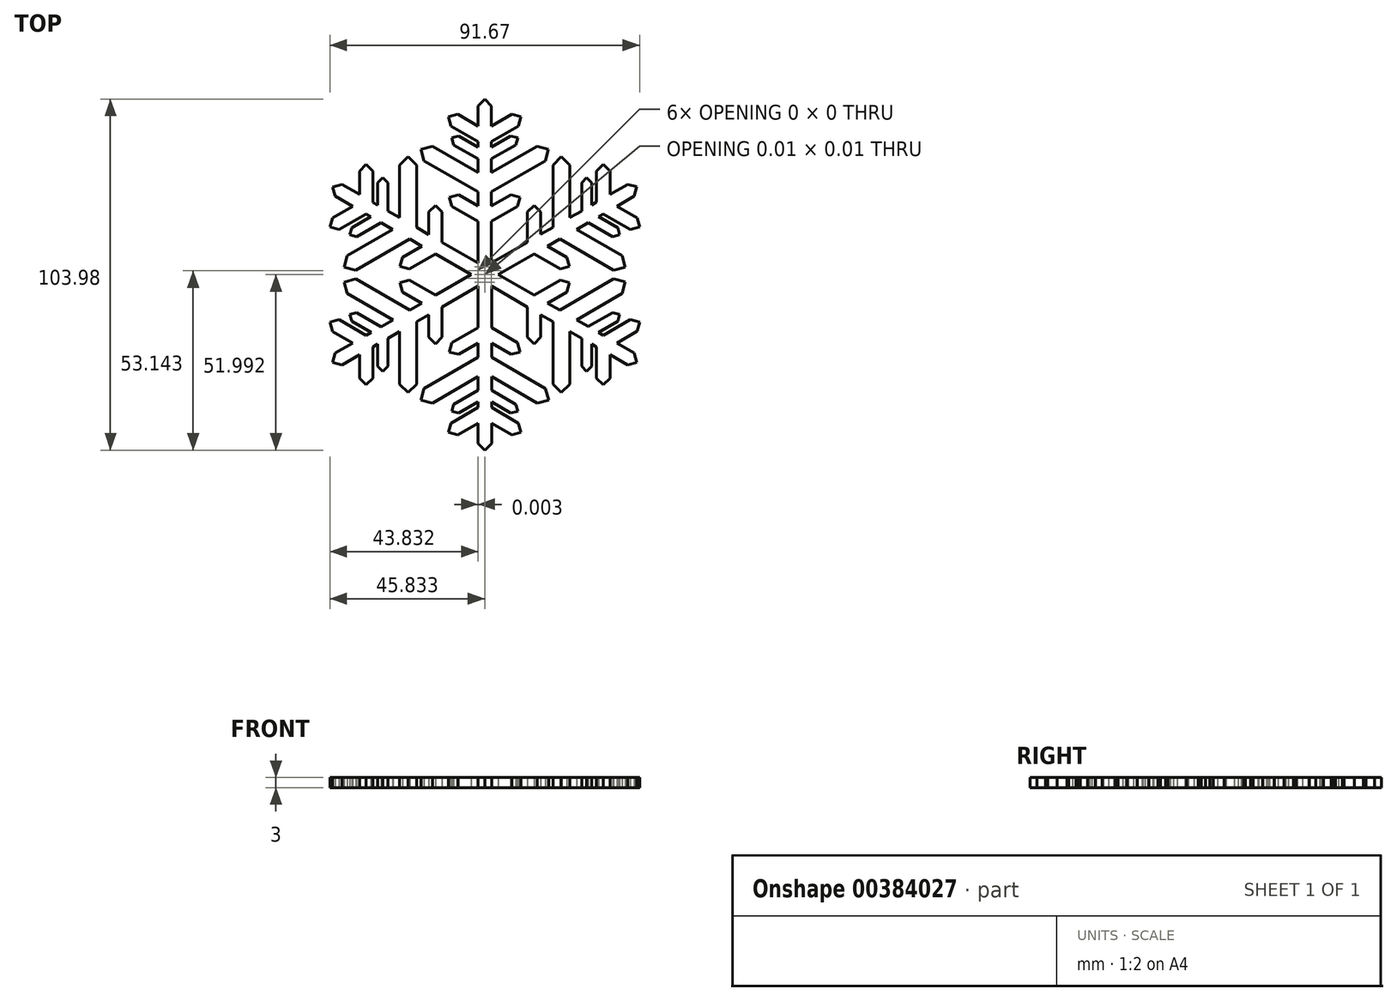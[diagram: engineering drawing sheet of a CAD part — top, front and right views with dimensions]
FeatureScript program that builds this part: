
annotation { "Feature Type Name" : "Feature", "Feature Type Description" : "" }
export const myFeature = defineFeature(function(context is Context, id is Id, definition is map)
    precondition{}
    {
        {
            var Q0;
            Q0=qCreatedBy(makeId("Top.planeOp"),FACE);
            var sketch = newSketch(context, id + "F0", { "sketchPlane" : qUnion([Q0])});
            skLineSegment(sketch, "E0", {"start": v(0, 26) * mm, "end": v(0, -26) * mm, "construction": true});
            skLineSegment(sketch, "E1", {"start": v(22.52, 13) * mm, "end": v(-22.52, -13) * mm, "construction": true});
            skLineSegment(sketch, "E2", {"start": v(22.52, -13) * mm, "end": v(-22.52, 13) * mm, "construction": true});
            skLineSegment(sketch, "E3", {"start": v(0, 0) * mm, "end": v(0, 26) * mm});
            skLineSegment(sketch, "E4", {"start": v(0, 26) * mm, "end": v(-1, 25) * mm});
            skLineSegment(sketch, "E5", {"start": v(-1, 25) * mm, "end": v(-1, 22) * mm});
            skLineSegment(sketch, "E6", {"start": v(-1, 22) * mm, "end": v(-4, 23.74) * mm});
            skLineSegment(sketch, "E7", {"start": v(-4, 23.74) * mm, "end": v(-5.37, 23.37) * mm});
            skLineSegment(sketch, "E8", {"start": v(-5.37, 23.37) * mm, "end": v(-5, 22) * mm});
            skLineSegment(sketch, "E9", {"start": v(-5, 22) * mm, "end": v(-1, 19.7) * mm});
            skLineSegment(sketch, "E10", {"start": v(-1, 19.7) * mm, "end": v(-1, 18.88) * mm});
            skLineSegment(sketch, "E11", {"start": v(-1, 18.88) * mm, "end": v(-3.86, 20.53) * mm});
            skLineSegment(sketch, "E12", {"start": v(-3.86, 20.53) * mm, "end": v(-4.88, 20.25) * mm});
            skLineSegment(sketch, "E13", {"start": v(-4.88, 20.25) * mm, "end": v(-4.6, 19.23) * mm});
            skLineSegment(sketch, "E14", {"start": v(-4.6, 19.23) * mm, "end": v(-1, 17.14) * mm});
            skLineSegment(sketch, "E15", {"start": v(-1, 17.14) * mm, "end": v(-1, 15.14) * mm});
            skLineSegment(sketch, "E16", {"start": v(-1, 15.14) * mm, "end": v(-7.74, 19.03) * mm});
            skLineSegment(sketch, "E17", {"start": v(-7.74, 19.03) * mm, "end": v(-9.45, 18.57) * mm});
            skLineSegment(sketch, "E18", {"start": v(-9.45, 18.57) * mm, "end": v(-9, 16.86) * mm});
            skLineSegment(sketch, "E19", {"start": v(-9, 16.86) * mm, "end": v(-1, 12.25) * mm});
            skLineSegment(sketch, "E20", {"start": v(-1, 12.25) * mm, "end": v(-1, 10.17) * mm});
            skLineSegment(sketch, "E21", {"start": v(-1, 10.17) * mm, "end": v(-3.87, 11.83) * mm});
            skLineSegment(sketch, "E22", {"start": v(-3.87, 11.83) * mm, "end": v(-5.23, 11.47) * mm});
            skLineSegment(sketch, "E23", {"start": v(-5.23, 11.47) * mm, "end": v(-4.87, 10.1) * mm});
            skLineSegment(sketch, "E24", {"start": v(-4.87, 10.1) * mm, "end": v(-1, 7.87) * mm});
            skLineSegment(sketch, "E25", {"start": v(-1, 7.87) * mm, "end": v(-1, 0.58) * mm});
            skLineSegment(sketch, "E26.MirrorCS", {"start": v(4.88, 20.25) * mm, "end": v(4.6, 19.23) * mm});
            skLineSegment(sketch, "E27.MirrorCS", {"start": v(5.23, 11.47) * mm, "end": v(4.87, 10.1) * mm});
            skLineSegment(sketch, "E28.MirrorCS", {"start": v(3.86, 20.53) * mm, "end": v(4.88, 20.25) * mm});
            skLineSegment(sketch, "E29.MirrorCS", {"start": v(1, 15.14) * mm, "end": v(7.74, 19.03) * mm});
            skLineSegment(sketch, "E30.MirrorCS", {"start": v(4.87, 10.1) * mm, "end": v(1, 7.87) * mm});
            skLineSegment(sketch, "E31.MirrorCS", {"start": v(1, 10.17) * mm, "end": v(3.87, 11.83) * mm});
            skLineSegment(sketch, "E32.MirrorCS", {"start": v(1, 17.14) * mm, "end": v(1, 15.14) * mm});
            skLineSegment(sketch, "E33.MirrorCS", {"start": v(4.6, 19.23) * mm, "end": v(1, 17.14) * mm});
            skLineSegment(sketch, "E34.MirrorCS", {"start": v(9.45, 18.57) * mm, "end": v(9, 16.86) * mm});
            skLineSegment(sketch, "E35.MirrorCS", {"start": v(1, 12.25) * mm, "end": v(1, 10.17) * mm});
            skLineSegment(sketch, "E36.MirrorCS", {"start": v(9, 16.86) * mm, "end": v(1, 12.25) * mm});
            skLineSegment(sketch, "E37.MirrorCS", {"start": v(0, 26) * mm, "end": v(1, 25) * mm});
            skLineSegment(sketch, "E38.MirrorCS", {"start": v(1, 22) * mm, "end": v(4, 23.74) * mm});
            skLineSegment(sketch, "E39.MirrorCS", {"start": v(1, 25) * mm, "end": v(1, 22) * mm});
            skLineSegment(sketch, "E40.MirrorCS", {"start": v(7.74, 19.03) * mm, "end": v(9.45, 18.57) * mm});
            skLineSegment(sketch, "E41.MirrorCS", {"start": v(1, 18.88) * mm, "end": v(3.86, 20.53) * mm});
            skLineSegment(sketch, "E42.MirrorCS", {"start": v(4, 23.74) * mm, "end": v(5.37, 23.37) * mm});
            skLineSegment(sketch, "E43.MirrorCS", {"start": v(5, 22) * mm, "end": v(1, 19.7) * mm});
            skLineSegment(sketch, "E44.MirrorCS", {"start": v(5.37, 23.37) * mm, "end": v(5, 22) * mm});
            skLineSegment(sketch, "E45.MirrorCS", {"start": v(1, 7.87) * mm, "end": v(1, 0.58) * mm});
            skLineSegment(sketch, "E46.MirrorCS", {"start": v(3.87, 11.83) * mm, "end": v(5.23, 11.47) * mm});
            skLineSegment(sketch, "E47.MirrorCS", {"start": v(1, 19.7) * mm, "end": v(1, 18.88) * mm});
            skLineSegment(sketch, "E48", {"start": v(-5, 22) * mm, "end": v(-4, 23.74) * mm, "construction": true});
            skLineSegment(sketch, "E49", {"start": v(-4.6, 19.23) * mm, "end": v(-3.86, 20.53) * mm, "construction": true});
            skLineSegment(sketch, "E50", {"start": v(-9, 16.86) * mm, "end": v(-7.74, 19.03) * mm, "construction": true});
            skLineSegment(sketch, "E51", {"start": v(-4.87, 10.1) * mm, "end": v(-3.87, 11.83) * mm, "construction": true});
            skLineSegment(sketch, "E52", {"start": v(-9.45, 18.57) * mm, "end": v(-8.37, 17.95) * mm, "construction": true});
            skLineSegment(sketch, "E53", {"start": v(-4.37, 10.97) * mm, "end": v(-5.23, 11.47) * mm, "construction": true});
            skLineSegment(sketch, "E54", {"start": v(-4.23, 19.88) * mm, "end": v(-4.88, 20.25) * mm, "construction": true});
            skLineSegment(sketch, "E55", {"start": v(-4.5, 22.87) * mm, "end": v(-5.37, 23.37) * mm, "construction": true});
            skLineSegment(sketch, "E56.1.0", {"start": v(-16.55, 15.33) * mm, "end": v(-16.55, 10.72) * mm});
            skLineSegment(sketch, "E56.1.1", {"start": v(-14.34, 9.44) * mm, "end": v(-12.6, 8.44) * mm});
            skLineSegment(sketch, "E56.1.2", {"start": v(-21.55, 6.67) * mm, "end": v(-17.55, 8.98) * mm});
            skLineSegment(sketch, "E56.1.3", {"start": v(-16.55, 10.72) * mm, "end": v(-15.84, 10.3) * mm});
            skLineSegment(sketch, "E56.1.4", {"start": v(-11.35, 17.47) * mm, "end": v(-10.1, 16.22) * mm});
            skLineSegment(sketch, "E56.1.5", {"start": v(-18.55, 15.33) * mm, "end": v(-17.55, 16.33) * mm});
            skLineSegment(sketch, "E56.1.6", {"start": v(-17.55, 16.33) * mm, "end": v(-16.55, 15.33) * mm});
            skLineSegment(sketch, "E56.1.7", {"start": v(-12.6, 16.22) * mm, "end": v(-11.35, 17.47) * mm});
            skLineSegment(sketch, "E56.1.8", {"start": v(-11.17, 0.83) * mm, "end": v(-7.3, 3.07) * mm});
            skLineSegment(sketch, "E56.1.9", {"start": v(-8.3, 9.27) * mm, "end": v(-7.3, 10.27) * mm});
            skLineSegment(sketch, "E56.1.10", {"start": v(-6.3, 9.27) * mm, "end": v(-6.3, 4.8) * mm});
            skLineSegment(sketch, "E56.1.11", {"start": v(-22.55, 8.4) * mm, "end": v(-22.92, 7.04) * mm});
            skLineSegment(sketch, "E56.1.12", {"start": v(-22.92, 7.04) * mm, "end": v(-21.55, 6.67) * mm});
            skLineSegment(sketch, "E56.1.13", {"start": v(-17.55, 8.98) * mm, "end": v(-16.84, 8.57) * mm});
            skLineSegment(sketch, "E56.1.14", {"start": v(-10.1, 16.22) * mm, "end": v(-10.1, 7) * mm});
            skLineSegment(sketch, "E56.1.15", {"start": v(-12.54, 1.2) * mm, "end": v(-11.17, 0.83) * mm});
            skLineSegment(sketch, "E56.1.16", {"start": v(-19.55, 10.14) * mm, "end": v(-22.55, 8.4) * mm});
            skLineSegment(sketch, "E56.1.17", {"start": v(-14.34, 13.6) * mm, "end": v(-14.34, 9.44) * mm});
            skLineSegment(sketch, "E56.1.18", {"start": v(-13.6, 6.7) * mm, "end": v(-20.34, 2.81) * mm});
            skLineSegment(sketch, "E56.1.19", {"start": v(-7.3, 3.07) * mm, "end": v(-1, -0.58) * mm});
            skLineSegment(sketch, "E56.1.20", {"start": v(-15.34, 7.7) * mm, "end": v(-13.6, 6.7) * mm});
            skLineSegment(sketch, "E56.1.21", {"start": v(-16.84, 8.57) * mm, "end": v(-19.7, 6.92) * mm});
            skLineSegment(sketch, "E56.1.22", {"start": v(-8.3, 5.96) * mm, "end": v(-8.3, 9.27) * mm});
            skLineSegment(sketch, "E56.1.23", {"start": v(-11.1, 5.26) * mm, "end": v(-9.3, 4.22) * mm});
            skLineSegment(sketch, "E56.1.24", {"start": v(-12.6, 8.44) * mm, "end": v(-12.6, 16.22) * mm});
            skLineSegment(sketch, "E56.1.25", {"start": v(-19.1, 0.65) * mm, "end": v(-11.1, 5.26) * mm});
            skLineSegment(sketch, "E56.1.26", {"start": v(-20.8, 1.1) * mm, "end": v(-19.1, 0.65) * mm});
            skLineSegment(sketch, "E56.1.27", {"start": v(-21.14, 13.37) * mm, "end": v(-18.55, 11.87) * mm});
            skLineSegment(sketch, "E56.1.28", {"start": v(-10.1, 7) * mm, "end": v(-8.3, 5.96) * mm});
            skLineSegment(sketch, "E56.1.29", {"start": v(-7.3, 10.27) * mm, "end": v(-6.3, 9.27) * mm});
            skLineSegment(sketch, "E56.1.30", {"start": v(-18.55, 11.87) * mm, "end": v(-18.55, 15.33) * mm});
            skLineSegment(sketch, "E56.1.31", {"start": v(-15.84, 10.3) * mm, "end": v(-15.84, 13.6) * mm});
            skLineSegment(sketch, "E56.1.32", {"start": v(-12.17, 2.57) * mm, "end": v(-12.54, 1.2) * mm});
            skLineSegment(sketch, "E56.1.33", {"start": v(-20.34, 2.81) * mm, "end": v(-20.8, 1.1) * mm});
            skLineSegment(sketch, "E56.1.34", {"start": v(-9.3, 4.22) * mm, "end": v(-12.17, 2.57) * mm});
            skLineSegment(sketch, "E56.1.35", {"start": v(-18.95, 5.63) * mm, "end": v(-15.34, 7.7) * mm});
            skLineSegment(sketch, "E56.1.36", {"start": v(-6.3, 4.8) * mm, "end": v(0, 1.16) * mm});
            skLineSegment(sketch, "E56.1.37", {"start": v(-22.14, 11.64) * mm, "end": v(-19.55, 10.14) * mm});
            skLineSegment(sketch, "E56.1.38", {"start": v(0, 0) * mm, "end": v(-22.51, 13) * mm});
            skLineSegment(sketch, "E56.1.39", {"start": v(-20.8, 1.1) * mm, "end": v(-19.72, 1.73) * mm, "construction": true});
            skLineSegment(sketch, "E56.1.40", {"start": v(-18.95, 5.63) * mm, "end": v(-19.7, 6.92) * mm, "construction": true});
            skLineSegment(sketch, "E56.1.41", {"start": v(-11.67, 1.7) * mm, "end": v(-12.54, 1.2) * mm, "construction": true});
            skLineSegment(sketch, "E56.1.42", {"start": v(-21.55, 6.67) * mm, "end": v(-22.55, 8.4) * mm, "construction": true});
            skLineSegment(sketch, "E56.1.43", {"start": v(-19.32, 6.28) * mm, "end": v(-19.97, 5.9) * mm, "construction": true});
            skLineSegment(sketch, "E56.1.44", {"start": v(-11.17, 0.83) * mm, "end": v(-12.17, 2.57) * mm, "construction": true});
            skLineSegment(sketch, "E56.1.45", {"start": v(-19.1, 0.65) * mm, "end": v(-20.34, 2.81) * mm, "construction": true});
            skLineSegment(sketch, "E56.1.46", {"start": v(-22.05, 7.54) * mm, "end": v(-22.92, 7.04) * mm, "construction": true});
            skLineSegment(sketch, "E56.1.47", {"start": v(-15.1, 14.35) * mm, "end": v(-14.34, 13.6) * mm});
            skLineSegment(sketch, "E56.1.48", {"start": v(-15.84, 13.6) * mm, "end": v(-15.1, 14.35) * mm});
            skLineSegment(sketch, "E56.1.49", {"start": v(-22.51, 13) * mm, "end": v(-21.14, 13.37) * mm});
            skLineSegment(sketch, "E56.1.50", {"start": v(-22.51, 13) * mm, "end": v(-22.14, 11.64) * mm});
            skLineSegment(sketch, "E56.1.51", {"start": v(-19.97, 5.9) * mm, "end": v(-18.95, 5.63) * mm});
            skLineSegment(sketch, "E56.1.52", {"start": v(-19.7, 6.92) * mm, "end": v(-19.97, 5.9) * mm});
            skLineSegment(sketch, "E56.2.0", {"start": v(-21.55, -6.66) * mm, "end": v(-17.55, -8.97) * mm});
            skLineSegment(sketch, "E56.2.1", {"start": v(-15.34, -7.7) * mm, "end": v(-13.6, -6.7) * mm});
            skLineSegment(sketch, "E56.2.2", {"start": v(-16.55, -15.33) * mm, "end": v(-16.55, -10.7) * mm});
            skLineSegment(sketch, "E56.2.3", {"start": v(-17.55, -8.97) * mm, "end": v(-16.84, -8.56) * mm});
            skLineSegment(sketch, "E56.2.4", {"start": v(-20.8, -1.1) * mm, "end": v(-19.1, -0.64) * mm});
            skLineSegment(sketch, "E56.2.5", {"start": v(-22.55, -8.4) * mm, "end": v(-22.92, -7.03) * mm});
            skLineSegment(sketch, "E56.2.6", {"start": v(-22.92, -7.03) * mm, "end": v(-21.55, -6.66) * mm});
            skLineSegment(sketch, "E56.2.7", {"start": v(-20.34, -2.8) * mm, "end": v(-20.8, -1.1) * mm});
            skLineSegment(sketch, "E56.2.8", {"start": v(-6.3, -9.26) * mm, "end": v(-6.3, -4.8) * mm});
            skLineSegment(sketch, "E56.2.9", {"start": v(-12.17, -2.56) * mm, "end": v(-12.54, -1.2) * mm});
            skLineSegment(sketch, "E56.2.10", {"start": v(-11.17, -0.83) * mm, "end": v(-7.3, -3.06) * mm});
            skLineSegment(sketch, "E56.2.11", {"start": v(-18.55, -15.33) * mm, "end": v(-17.55, -16.33) * mm});
            skLineSegment(sketch, "E56.2.12", {"start": v(-17.55, -16.33) * mm, "end": v(-16.55, -15.33) * mm});
            skLineSegment(sketch, "E56.2.13", {"start": v(-16.55, -10.7) * mm, "end": v(-15.84, -10.3) * mm});
            skLineSegment(sketch, "E56.2.14", {"start": v(-19.1, -0.64) * mm, "end": v(-11.1, -5.25) * mm});
            skLineSegment(sketch, "E56.2.15", {"start": v(-7.3, -10.26) * mm, "end": v(-6.3, -9.26) * mm});
            skLineSegment(sketch, "E56.2.16", {"start": v(-18.55, -11.86) * mm, "end": v(-18.55, -15.33) * mm});
            skLineSegment(sketch, "E56.2.17", {"start": v(-18.95, -5.62) * mm, "end": v(-15.34, -7.7) * mm});
            skLineSegment(sketch, "E56.2.18", {"start": v(-12.6, -8.43) * mm, "end": v(-12.6, -16.2) * mm});
            skLineSegment(sketch, "E56.2.19", {"start": v(-6.3, -4.8) * mm, "end": v(0, -1.15) * mm});
            skLineSegment(sketch, "E56.2.20", {"start": v(-14.34, -9.43) * mm, "end": v(-12.6, -8.43) * mm});
            skLineSegment(sketch, "E56.2.21", {"start": v(-15.84, -10.3) * mm, "end": v(-15.84, -13.6) * mm});
            skLineSegment(sketch, "E56.2.22", {"start": v(-9.3, -4.21) * mm, "end": v(-12.17, -2.56) * mm});
            skLineSegment(sketch, "E56.2.23", {"start": v(-10.1, -6.98) * mm, "end": v(-8.3, -5.95) * mm});
            skLineSegment(sketch, "E56.2.24", {"start": v(-13.6, -6.7) * mm, "end": v(-20.34, -2.8) * mm});
            skLineSegment(sketch, "E56.2.25", {"start": v(-10.1, -16.2) * mm, "end": v(-10.1, -6.98) * mm});
            skLineSegment(sketch, "E56.2.26", {"start": v(-11.35, -17.46) * mm, "end": v(-10.1, -16.2) * mm});
            skLineSegment(sketch, "E56.2.27", {"start": v(-22.14, -11.63) * mm, "end": v(-19.55, -10.13) * mm});
            skLineSegment(sketch, "E56.2.28", {"start": v(-11.1, -5.25) * mm, "end": v(-9.3, -4.21) * mm});
            skLineSegment(sketch, "E56.2.29", {"start": v(-12.54, -1.2) * mm, "end": v(-11.17, -0.83) * mm});
            skLineSegment(sketch, "E56.2.30", {"start": v(-19.55, -10.13) * mm, "end": v(-22.55, -8.4) * mm});
            skLineSegment(sketch, "E56.2.31", {"start": v(-16.84, -8.56) * mm, "end": v(-19.7, -6.92) * mm});
            skLineSegment(sketch, "E56.2.32", {"start": v(-8.3, -9.26) * mm, "end": v(-7.3, -10.26) * mm});
            skLineSegment(sketch, "E56.2.33", {"start": v(-12.6, -16.2) * mm, "end": v(-11.35, -17.46) * mm});
            skLineSegment(sketch, "E56.2.34", {"start": v(-8.3, -5.95) * mm, "end": v(-8.3, -9.26) * mm});
            skLineSegment(sketch, "E56.2.35", {"start": v(-14.34, -13.6) * mm, "end": v(-14.34, -9.43) * mm});
            skLineSegment(sketch, "E56.2.36", {"start": v(-7.3, -3.06) * mm, "end": v(-1, 0.59) * mm});
            skLineSegment(sketch, "E56.2.37", {"start": v(-21.14, -13.36) * mm, "end": v(-18.55, -11.86) * mm});
            skLineSegment(sketch, "E56.2.38", {"start": v(0, 0) * mm, "end": v(-22.5, -13) * mm});
            skLineSegment(sketch, "E56.2.39", {"start": v(-11.35, -17.46) * mm, "end": v(-11.35, -16.2) * mm, "construction": true});
            skLineSegment(sketch, "E56.2.40", {"start": v(-14.34, -13.6) * mm, "end": v(-15.84, -13.6) * mm, "construction": true});
            skLineSegment(sketch, "E56.2.41", {"start": v(-7.3, -9.26) * mm, "end": v(-7.3, -10.26) * mm, "construction": true});
            skLineSegment(sketch, "E56.2.42", {"start": v(-16.55, -15.33) * mm, "end": v(-18.55, -15.33) * mm, "construction": true});
            skLineSegment(sketch, "E56.2.43", {"start": v(-15.09, -13.6) * mm, "end": v(-15.09, -14.34) * mm, "construction": true});
            skLineSegment(sketch, "E56.2.44", {"start": v(-6.3, -9.26) * mm, "end": v(-8.3, -9.26) * mm, "construction": true});
            skLineSegment(sketch, "E56.2.45", {"start": v(-10.1, -16.2) * mm, "end": v(-12.6, -16.2) * mm, "construction": true});
            skLineSegment(sketch, "E56.2.46", {"start": v(-17.55, -15.33) * mm, "end": v(-17.55, -16.33) * mm, "construction": true});
            skLineSegment(sketch, "E56.2.47", {"start": v(-19.97, -5.9) * mm, "end": v(-18.95, -5.62) * mm});
            skLineSegment(sketch, "E56.2.48", {"start": v(-19.7, -6.92) * mm, "end": v(-19.97, -5.9) * mm});
            skLineSegment(sketch, "E56.2.49", {"start": v(-22.5, -13) * mm, "end": v(-22.14, -11.63) * mm});
            skLineSegment(sketch, "E56.2.50", {"start": v(-22.5, -13) * mm, "end": v(-21.14, -13.36) * mm});
            skLineSegment(sketch, "E56.2.51", {"start": v(-15.09, -14.34) * mm, "end": v(-14.34, -13.6) * mm});
            skLineSegment(sketch, "E56.2.52", {"start": v(-15.84, -13.6) * mm, "end": v(-15.09, -14.34) * mm});
            skLineSegment(sketch, "E56.3.0", {"start": v(-5, -22) * mm, "end": v(-1, -19.68) * mm});
            skLineSegment(sketch, "E56.3.1", {"start": v(-1, -17.13) * mm, "end": v(-1, -15.12) * mm});
            skLineSegment(sketch, "E56.3.2", {"start": v(5, -22) * mm, "end": v(1, -19.68) * mm});
            skLineSegment(sketch, "E56.3.3", {"start": v(-1, -19.68) * mm, "end": v(-1, -18.86) * mm});
            skLineSegment(sketch, "E56.3.4", {"start": v(-9.44, -18.56) * mm, "end": v(-8.99, -16.85) * mm});
            skLineSegment(sketch, "E56.3.5", {"start": v(-4, -23.73) * mm, "end": v(-5.36, -23.36) * mm});
            skLineSegment(sketch, "E56.3.6", {"start": v(-5.36, -23.36) * mm, "end": v(-5, -22) * mm});
            skLineSegment(sketch, "E56.3.7", {"start": v(-7.74, -19.02) * mm, "end": v(-9.44, -18.56) * mm});
            skLineSegment(sketch, "E56.3.8", {"start": v(4.87, -10.09) * mm, "end": v(1, -7.85) * mm});
            skLineSegment(sketch, "E56.3.9", {"start": v(-3.87, -11.82) * mm, "end": v(-5.23, -11.45) * mm});
            skLineSegment(sketch, "E56.3.10", {"start": v(-4.87, -10.09) * mm, "end": v(-1, -7.85) * mm});
            skLineSegment(sketch, "E56.3.11", {"start": v(4, -23.73) * mm, "end": v(5.37, -23.36) * mm});
            skLineSegment(sketch, "E56.3.12", {"start": v(5.37, -23.36) * mm, "end": v(5, -22) * mm});
            skLineSegment(sketch, "E56.3.13", {"start": v(1, -19.68) * mm, "end": v(1, -18.86) * mm});
            skLineSegment(sketch, "E56.3.14", {"start": v(-8.99, -16.85) * mm, "end": v(-1, -12.24) * mm});
            skLineSegment(sketch, "E56.3.15", {"start": v(5.24, -11.45) * mm, "end": v(4.87, -10.09) * mm});
            skLineSegment(sketch, "E56.3.16", {"start": v(1, -22) * mm, "end": v(4, -23.73) * mm});
            skLineSegment(sketch, "E56.3.17", {"start": v(-4.6, -19.21) * mm, "end": v(-1, -17.13) * mm});
            skLineSegment(sketch, "E56.3.18", {"start": v(1, -15.12) * mm, "end": v(7.74, -19.02) * mm});
            skLineSegment(sketch, "E56.3.19", {"start": v(1, -7.85) * mm, "end": v(1, -0.57) * mm});
            skLineSegment(sketch, "E56.3.20", {"start": v(1, -17.13) * mm, "end": v(1, -15.12) * mm});
            skLineSegment(sketch, "E56.3.21", {"start": v(1, -18.86) * mm, "end": v(3.86, -20.51) * mm});
            skLineSegment(sketch, "E56.3.22", {"start": v(-1, -10.16) * mm, "end": v(-3.87, -11.82) * mm});
            skLineSegment(sketch, "E56.3.23", {"start": v(1, -12.24) * mm, "end": v(1, -10.16) * mm});
            skLineSegment(sketch, "E56.3.24", {"start": v(-1, -15.12) * mm, "end": v(-7.74, -19.02) * mm});
            skLineSegment(sketch, "E56.3.25", {"start": v(9, -16.85) * mm, "end": v(1, -12.24) * mm});
            skLineSegment(sketch, "E56.3.26", {"start": v(9.45, -18.56) * mm, "end": v(9, -16.85) * mm});
            skLineSegment(sketch, "E56.3.27", {"start": v(-1, -24.99) * mm, "end": v(-1, -22) * mm});
            skLineSegment(sketch, "E56.3.28", {"start": v(-1, -12.24) * mm, "end": v(-1, -10.16) * mm});
            skLineSegment(sketch, "E56.3.29", {"start": v(-5.23, -11.45) * mm, "end": v(-4.87, -10.09) * mm});
            skLineSegment(sketch, "E56.3.30", {"start": v(-1, -22) * mm, "end": v(-4, -23.73) * mm});
            skLineSegment(sketch, "E56.3.31", {"start": v(-1, -18.86) * mm, "end": v(-3.85, -20.51) * mm});
            skLineSegment(sketch, "E56.3.32", {"start": v(3.87, -11.82) * mm, "end": v(5.24, -11.45) * mm});
            skLineSegment(sketch, "E56.3.33", {"start": v(7.74, -19.02) * mm, "end": v(9.45, -18.56) * mm});
            skLineSegment(sketch, "E56.3.34", {"start": v(1, -10.16) * mm, "end": v(3.87, -11.82) * mm});
            skLineSegment(sketch, "E56.3.35", {"start": v(4.6, -19.21) * mm, "end": v(1, -17.13) * mm});
            skLineSegment(sketch, "E56.3.36", {"start": v(-1, -7.85) * mm, "end": v(-1, -0.57) * mm});
            skLineSegment(sketch, "E56.3.37", {"start": v(1, -24.99) * mm, "end": v(1, -22) * mm});
            skLineSegment(sketch, "E56.3.38", {"start": v(0, 0.01) * mm, "end": v(0, -25.99) * mm});
            skLineSegment(sketch, "E56.3.39", {"start": v(9.45, -18.56) * mm, "end": v(8.37, -17.93) * mm, "construction": true});
            skLineSegment(sketch, "E56.3.40", {"start": v(4.6, -19.21) * mm, "end": v(3.86, -20.51) * mm, "construction": true});
            skLineSegment(sketch, "E56.3.41", {"start": v(4.37, -10.95) * mm, "end": v(5.24, -11.45) * mm, "construction": true});
            skLineSegment(sketch, "E56.3.42", {"start": v(5, -22) * mm, "end": v(4, -23.73) * mm, "construction": true});
            skLineSegment(sketch, "E56.3.43", {"start": v(4.23, -19.86) * mm, "end": v(4.88, -20.24) * mm, "construction": true});
            skLineSegment(sketch, "E56.3.44", {"start": v(4.87, -10.09) * mm, "end": v(3.87, -11.82) * mm, "construction": true});
            skLineSegment(sketch, "E56.3.45", {"start": v(9, -16.85) * mm, "end": v(7.74, -19.02) * mm, "construction": true});
            skLineSegment(sketch, "E56.3.46", {"start": v(4.5, -22.86) * mm, "end": v(5.37, -23.36) * mm, "construction": true});
            skLineSegment(sketch, "E56.3.47", {"start": v(-4.88, -20.24) * mm, "end": v(-4.6, -19.21) * mm});
            skLineSegment(sketch, "E56.3.48", {"start": v(-3.85, -20.51) * mm, "end": v(-4.88, -20.24) * mm});
            skLineSegment(sketch, "E56.3.49", {"start": v(0, -25.99) * mm, "end": v(-1, -24.99) * mm});
            skLineSegment(sketch, "E56.3.50", {"start": v(0, -25.99) * mm, "end": v(1, -24.99) * mm});
            skLineSegment(sketch, "E56.3.51", {"start": v(4.88, -20.24) * mm, "end": v(4.6, -19.21) * mm});
            skLineSegment(sketch, "E56.3.52", {"start": v(3.86, -20.51) * mm, "end": v(4.88, -20.24) * mm});
            skLineSegment(sketch, "E56.4.0", {"start": v(16.55, -15.32) * mm, "end": v(16.55, -10.7) * mm});
            skLineSegment(sketch, "E56.4.1", {"start": v(14.34, -9.43) * mm, "end": v(12.6, -8.42) * mm});
            skLineSegment(sketch, "E56.4.2", {"start": v(21.55, -6.66) * mm, "end": v(17.55, -8.97) * mm});
            skLineSegment(sketch, "E56.4.3", {"start": v(16.55, -10.7) * mm, "end": v(15.84, -10.3) * mm});
            skLineSegment(sketch, "E56.4.4", {"start": v(11.36, -17.46) * mm, "end": v(10.1, -16.2) * mm});
            skLineSegment(sketch, "E56.4.5", {"start": v(18.55, -15.32) * mm, "end": v(17.55, -16.32) * mm});
            skLineSegment(sketch, "E56.4.6", {"start": v(17.55, -16.32) * mm, "end": v(16.55, -15.32) * mm});
            skLineSegment(sketch, "E56.4.7", {"start": v(12.6, -16.2) * mm, "end": v(11.36, -17.46) * mm});
            skLineSegment(sketch, "E56.4.8", {"start": v(11.18, -0.82) * mm, "end": v(7.3, -3.06) * mm});
            skLineSegment(sketch, "E56.4.9", {"start": v(8.3, -9.26) * mm, "end": v(7.3, -10.26) * mm});
            skLineSegment(sketch, "E56.4.10", {"start": v(6.3, -9.26) * mm, "end": v(6.3, -4.79) * mm});
            skLineSegment(sketch, "E56.4.11", {"start": v(22.55, -8.4) * mm, "end": v(22.92, -7.03) * mm});
            skLineSegment(sketch, "E56.4.12", {"start": v(22.92, -7.03) * mm, "end": v(21.55, -6.66) * mm});
            skLineSegment(sketch, "E56.4.13", {"start": v(17.55, -8.97) * mm, "end": v(16.84, -8.56) * mm});
            skLineSegment(sketch, "E56.4.14", {"start": v(10.1, -16.2) * mm, "end": v(10.1, -6.98) * mm});
            skLineSegment(sketch, "E56.4.15", {"start": v(12.54, -1.19) * mm, "end": v(11.18, -0.82) * mm});
            skLineSegment(sketch, "E56.4.16", {"start": v(19.55, -10.13) * mm, "end": v(22.55, -8.4) * mm});
            skLineSegment(sketch, "E56.4.17", {"start": v(14.34, -13.6) * mm, "end": v(14.34, -9.43) * mm});
            skLineSegment(sketch, "E56.4.18", {"start": v(13.6, -6.7) * mm, "end": v(20.35, -2.8) * mm});
            skLineSegment(sketch, "E56.4.19", {"start": v(7.3, -3.06) * mm, "end": v(1, 0.59) * mm});
            skLineSegment(sketch, "E56.4.20", {"start": v(15.34, -7.7) * mm, "end": v(13.6, -6.7) * mm});
            skLineSegment(sketch, "E56.4.21", {"start": v(16.84, -8.56) * mm, "end": v(19.7, -6.91) * mm});
            skLineSegment(sketch, "E56.4.22", {"start": v(8.3, -5.94) * mm, "end": v(8.3, -9.26) * mm});
            skLineSegment(sketch, "E56.4.23", {"start": v(11.1, -5.25) * mm, "end": v(9.3, -4.21) * mm});
            skLineSegment(sketch, "E56.4.24", {"start": v(12.6, -8.42) * mm, "end": v(12.6, -16.2) * mm});
            skLineSegment(sketch, "E56.4.25", {"start": v(19.1, -0.64) * mm, "end": v(11.1, -5.25) * mm});
            skLineSegment(sketch, "E56.4.26", {"start": v(20.8, -1.1) * mm, "end": v(19.1, -0.64) * mm});
            skLineSegment(sketch, "E56.4.27", {"start": v(21.15, -13.36) * mm, "end": v(18.55, -11.86) * mm});
            skLineSegment(sketch, "E56.4.28", {"start": v(10.1, -6.98) * mm, "end": v(8.3, -5.94) * mm});
            skLineSegment(sketch, "E56.4.29", {"start": v(7.3, -10.26) * mm, "end": v(6.3, -9.26) * mm});
            skLineSegment(sketch, "E56.4.30", {"start": v(18.55, -11.86) * mm, "end": v(18.55, -15.32) * mm});
            skLineSegment(sketch, "E56.4.31", {"start": v(15.84, -10.3) * mm, "end": v(15.84, -13.6) * mm});
            skLineSegment(sketch, "E56.4.32", {"start": v(12.18, -2.55) * mm, "end": v(12.54, -1.19) * mm});
            skLineSegment(sketch, "E56.4.33", {"start": v(20.35, -2.8) * mm, "end": v(20.8, -1.1) * mm});
            skLineSegment(sketch, "E56.4.34", {"start": v(9.3, -4.21) * mm, "end": v(12.18, -2.55) * mm});
            skLineSegment(sketch, "E56.4.35", {"start": v(18.95, -5.61) * mm, "end": v(15.34, -7.7) * mm});
            skLineSegment(sketch, "E56.4.36", {"start": v(6.3, -4.79) * mm, "end": v(0, -1.14) * mm});
            skLineSegment(sketch, "E56.4.37", {"start": v(22.15, -11.62) * mm, "end": v(19.55, -10.13) * mm});
            skLineSegment(sketch, "E56.4.38", {"start": v(0, 0.01) * mm, "end": v(22.51, -12.99) * mm});
            skLineSegment(sketch, "E56.4.39", {"start": v(20.8, -1.1) * mm, "end": v(19.72, -1.72) * mm, "construction": true});
            skLineSegment(sketch, "E56.4.40", {"start": v(18.95, -5.61) * mm, "end": v(19.7, -6.91) * mm, "construction": true});
            skLineSegment(sketch, "E56.4.41", {"start": v(11.68, -1.69) * mm, "end": v(12.54, -1.19) * mm, "construction": true});
            skLineSegment(sketch, "E56.4.42", {"start": v(21.55, -6.66) * mm, "end": v(22.55, -8.4) * mm, "construction": true});
            skLineSegment(sketch, "E56.4.43", {"start": v(19.33, -6.26) * mm, "end": v(19.98, -5.89) * mm, "construction": true});
            skLineSegment(sketch, "E56.4.44", {"start": v(11.18, -0.82) * mm, "end": v(12.18, -2.55) * mm, "construction": true});
            skLineSegment(sketch, "E56.4.45", {"start": v(19.1, -0.64) * mm, "end": v(20.35, -2.8) * mm, "construction": true});
            skLineSegment(sketch, "E56.4.46", {"start": v(22.05, -7.53) * mm, "end": v(22.92, -7.03) * mm, "construction": true});
            skLineSegment(sketch, "E56.4.47", {"start": v(15.1, -14.34) * mm, "end": v(14.34, -13.6) * mm});
            skLineSegment(sketch, "E56.4.48", {"start": v(15.84, -13.6) * mm, "end": v(15.1, -14.34) * mm});
            skLineSegment(sketch, "E56.4.49", {"start": v(22.51, -12.99) * mm, "end": v(21.15, -13.36) * mm});
            skLineSegment(sketch, "E56.4.50", {"start": v(22.51, -12.99) * mm, "end": v(22.15, -11.62) * mm});
            skLineSegment(sketch, "E56.4.51", {"start": v(19.98, -5.89) * mm, "end": v(18.95, -5.61) * mm});
            skLineSegment(sketch, "E56.4.52", {"start": v(19.7, -6.91) * mm, "end": v(19.98, -5.89) * mm});
            skLineSegment(sketch, "E56.5.0", {"start": v(21.55, 6.68) * mm, "end": v(17.55, 8.99) * mm});
            skLineSegment(sketch, "E56.5.1", {"start": v(15.34, 7.71) * mm, "end": v(13.6, 6.7) * mm});
            skLineSegment(sketch, "E56.5.2", {"start": v(16.55, 15.34) * mm, "end": v(16.55, 10.72) * mm});
            skLineSegment(sketch, "E56.5.3", {"start": v(17.55, 8.99) * mm, "end": v(16.84, 8.58) * mm});
            skLineSegment(sketch, "E56.5.4", {"start": v(20.8, 1.1) * mm, "end": v(19.1, 0.65) * mm});
            skLineSegment(sketch, "E56.5.5", {"start": v(22.55, 8.4) * mm, "end": v(22.92, 7.04) * mm});
            skLineSegment(sketch, "E56.5.6", {"start": v(22.92, 7.04) * mm, "end": v(21.55, 6.68) * mm});
            skLineSegment(sketch, "E56.5.7", {"start": v(20.34, 2.81) * mm, "end": v(20.8, 1.1) * mm});
            skLineSegment(sketch, "E56.5.8", {"start": v(6.3, 9.27) * mm, "end": v(6.3, 4.8) * mm});
            skLineSegment(sketch, "E56.5.9", {"start": v(12.18, 2.57) * mm, "end": v(12.54, 1.2) * mm});
            skLineSegment(sketch, "E56.5.10", {"start": v(11.18, 0.84) * mm, "end": v(7.3, 3.07) * mm});
            skLineSegment(sketch, "E56.5.11", {"start": v(18.55, 15.34) * mm, "end": v(17.55, 16.34) * mm});
            skLineSegment(sketch, "E56.5.12", {"start": v(17.55, 16.34) * mm, "end": v(16.55, 15.34) * mm});
            skLineSegment(sketch, "E56.5.13", {"start": v(16.55, 10.72) * mm, "end": v(15.84, 10.3) * mm});
            skLineSegment(sketch, "E56.5.14", {"start": v(19.1, 0.65) * mm, "end": v(11.1, 5.26) * mm});
            skLineSegment(sketch, "E56.5.15", {"start": v(7.3, 10.27) * mm, "end": v(6.3, 9.27) * mm});
            skLineSegment(sketch, "E56.5.16", {"start": v(18.55, 11.87) * mm, "end": v(18.55, 15.34) * mm});
            skLineSegment(sketch, "E56.5.17", {"start": v(18.95, 5.63) * mm, "end": v(15.34, 7.71) * mm});
            skLineSegment(sketch, "E56.5.18", {"start": v(12.6, 8.44) * mm, "end": v(12.6, 16.22) * mm});
            skLineSegment(sketch, "E56.5.19", {"start": v(6.3, 4.8) * mm, "end": v(0, 1.16) * mm});
            skLineSegment(sketch, "E56.5.20", {"start": v(14.34, 9.44) * mm, "end": v(12.6, 8.44) * mm});
            skLineSegment(sketch, "E56.5.21", {"start": v(15.84, 10.3) * mm, "end": v(15.84, 13.6) * mm});
            skLineSegment(sketch, "E56.5.22", {"start": v(9.3, 4.23) * mm, "end": v(12.18, 2.57) * mm});
            skLineSegment(sketch, "E56.5.23", {"start": v(10.1, 7) * mm, "end": v(8.3, 5.96) * mm});
            skLineSegment(sketch, "E56.5.24", {"start": v(13.6, 6.7) * mm, "end": v(20.34, 2.81) * mm});
            skLineSegment(sketch, "E56.5.25", {"start": v(10.1, 16.22) * mm, "end": v(10.1, 7) * mm});
            skLineSegment(sketch, "E56.5.26", {"start": v(11.35, 17.47) * mm, "end": v(10.1, 16.22) * mm});
            skLineSegment(sketch, "E56.5.27", {"start": v(22.15, 11.64) * mm, "end": v(19.55, 10.14) * mm});
            skLineSegment(sketch, "E56.5.28", {"start": v(11.1, 5.26) * mm, "end": v(9.3, 4.23) * mm});
            skLineSegment(sketch, "E56.5.29", {"start": v(12.54, 1.2) * mm, "end": v(11.18, 0.84) * mm});
            skLineSegment(sketch, "E56.5.30", {"start": v(19.55, 10.14) * mm, "end": v(22.55, 8.4) * mm});
            skLineSegment(sketch, "E56.5.31", {"start": v(16.84, 8.58) * mm, "end": v(19.7, 6.93) * mm});
            skLineSegment(sketch, "E56.5.32", {"start": v(8.3, 9.27) * mm, "end": v(7.3, 10.27) * mm});
            skLineSegment(sketch, "E56.5.33", {"start": v(12.6, 16.22) * mm, "end": v(11.35, 17.47) * mm});
            skLineSegment(sketch, "E56.5.34", {"start": v(8.3, 5.96) * mm, "end": v(8.3, 9.27) * mm});
            skLineSegment(sketch, "E56.5.35", {"start": v(14.34, 13.6) * mm, "end": v(14.34, 9.44) * mm});
            skLineSegment(sketch, "E56.5.36", {"start": v(7.3, 3.07) * mm, "end": v(1, -0.57) * mm});
            skLineSegment(sketch, "E56.5.37", {"start": v(21.15, 13.37) * mm, "end": v(18.55, 11.87) * mm});
            skLineSegment(sketch, "E56.5.38", {"start": v(0, 0) * mm, "end": v(22.51, 13) * mm});
            skLineSegment(sketch, "E56.5.39", {"start": v(11.35, 17.47) * mm, "end": v(11.35, 16.22) * mm, "construction": true});
            skLineSegment(sketch, "E56.5.40", {"start": v(14.34, 13.6) * mm, "end": v(15.84, 13.6) * mm, "construction": true});
            skLineSegment(sketch, "E56.5.41", {"start": v(7.3, 9.27) * mm, "end": v(7.3, 10.27) * mm, "construction": true});
            skLineSegment(sketch, "E56.5.42", {"start": v(16.55, 15.34) * mm, "end": v(18.55, 15.34) * mm, "construction": true});
            skLineSegment(sketch, "E56.5.43", {"start": v(15.1, 13.6) * mm, "end": v(15.1, 14.36) * mm, "construction": true});
            skLineSegment(sketch, "E56.5.44", {"start": v(6.3, 9.27) * mm, "end": v(8.3, 9.27) * mm, "construction": true});
            skLineSegment(sketch, "E56.5.45", {"start": v(10.1, 16.22) * mm, "end": v(12.6, 16.22) * mm, "construction": true});
            skLineSegment(sketch, "E56.5.46", {"start": v(17.55, 15.34) * mm, "end": v(17.55, 16.34) * mm, "construction": true});
            skLineSegment(sketch, "E56.5.47", {"start": v(19.97, 5.9) * mm, "end": v(18.95, 5.63) * mm});
            skLineSegment(sketch, "E56.5.48", {"start": v(19.7, 6.93) * mm, "end": v(19.97, 5.9) * mm});
            skLineSegment(sketch, "E56.5.49", {"start": v(22.51, 13) * mm, "end": v(22.15, 11.64) * mm});
            skLineSegment(sketch, "E56.5.50", {"start": v(22.51, 13) * mm, "end": v(21.15, 13.37) * mm});
            skLineSegment(sketch, "E56.5.51", {"start": v(15.1, 14.36) * mm, "end": v(14.34, 13.6) * mm});
            skLineSegment(sketch, "E56.5.52", {"start": v(15.84, 13.6) * mm, "end": v(15.1, 14.36) * mm});
            skPoint(sketch, "E56.center", {"position": v(0, 0) * mm});
            skSolve(sketch);
        }
        {
            var Q0;
            Q0 = qSketchRegion(id + "F0", true);
            extrude(context, id + "F1", {"entities" : qUnion([Q0]), "depth" : 1.5 * mm});
        }
        {
            var Q0;
            Q0=makeQuery(id+"F1.opExtrude","SWEPT_BODY",BODY,{"disambiguationData":[OSD([sQuery(id+"F0.wireOp",EDGE,"E3"),sQuery(id+"F0.wireOp",EDGE,"E4"),sQuery(id+"F0.wireOp",EDGE,"E5"),sQuery(id+"F0.wireOp",EDGE,"E6"),sQuery(id+"F0.wireOp",EDGE,"E7"),sQuery(id+"F0.wireOp",EDGE,"E8"),sQuery(id+"F0.wireOp",EDGE,"E9"),sQuery(id+"F0.wireOp",EDGE,"E10"),sQuery(id+"F0.wireOp",EDGE,"E11"),sQuery(id+"F0.wireOp",EDGE,"E12"),sQuery(id+"F0.wireOp",EDGE,"E13"),sQuery(id+"F0.wireOp",EDGE,"E14"),sQuery(id+"F0.wireOp",EDGE,"E15"),sQuery(id+"F0.wireOp",EDGE,"E16"),sQuery(id+"F0.wireOp",EDGE,"E17"),sQuery(id+"F0.wireOp",EDGE,"E18"),sQuery(id+"F0.wireOp",EDGE,"E19"),sQuery(id+"F0.wireOp",EDGE,"E20"),sQuery(id+"F0.wireOp",EDGE,"E21"),sQuery(id+"F0.wireOp",EDGE,"E22"),sQuery(id+"F0.wireOp",EDGE,"E23"),sQuery(id+"F0.wireOp",EDGE,"E24"),sQuery(id+"F0.wireOp",EDGE,"E25"),sQuery(id+"F0.wireOp",EDGE,"E26.MirrorCS"),sQuery(id+"F0.wireOp",EDGE,"E27.MirrorCS"),sQuery(id+"F0.wireOp",EDGE,"E28.MirrorCS"),sQuery(id+"F0.wireOp",EDGE,"E29.MirrorCS"),sQuery(id+"F0.wireOp",EDGE,"E30.MirrorCS"),sQuery(id+"F0.wireOp",EDGE,"E31.MirrorCS"),sQuery(id+"F0.wireOp",EDGE,"E32.MirrorCS"),sQuery(id+"F0.wireOp",EDGE,"E33.MirrorCS"),sQuery(id+"F0.wireOp",EDGE,"E34.MirrorCS"),sQuery(id+"F0.wireOp",EDGE,"E35.MirrorCS"),sQuery(id+"F0.wireOp",EDGE,"E36.MirrorCS"),sQuery(id+"F0.wireOp",EDGE,"E37.MirrorCS"),sQuery(id+"F0.wireOp",EDGE,"E38.MirrorCS"),sQuery(id+"F0.wireOp",EDGE,"E39.MirrorCS"),sQuery(id+"F0.wireOp",EDGE,"E40.MirrorCS"),sQuery(id+"F0.wireOp",EDGE,"E41.MirrorCS"),sQuery(id+"F0.wireOp",EDGE,"E42.MirrorCS"),sQuery(id+"F0.wireOp",EDGE,"E43.MirrorCS"),sQuery(id+"F0.wireOp",EDGE,"E44.MirrorCS"),sQuery(id+"F0.wireOp",EDGE,"E45.MirrorCS"),sQuery(id+"F0.wireOp",EDGE,"E46.MirrorCS"),sQuery(id+"F0.wireOp",EDGE,"E47.MirrorCS"),sQuery(id+"F0.wireOp",EDGE,"E56.1.0"),sQuery(id+"F0.wireOp",EDGE,"E56.1.1"),sQuery(id+"F0.wireOp",EDGE,"E56.1.2"),sQuery(id+"F0.wireOp",EDGE,"E56.1.3"),sQuery(id+"F0.wireOp",EDGE,"E56.1.4"),sQuery(id+"F0.wireOp",EDGE,"E56.1.5"),sQuery(id+"F0.wireOp",EDGE,"E56.1.6"),sQuery(id+"F0.wireOp",EDGE,"E56.1.7"),sQuery(id+"F0.wireOp",EDGE,"E56.1.8"),sQuery(id+"F0.wireOp",EDGE,"E56.1.9"),sQuery(id+"F0.wireOp",EDGE,"E56.1.10"),sQuery(id+"F0.wireOp",EDGE,"E56.1.11"),sQuery(id+"F0.wireOp",EDGE,"E56.1.12"),sQuery(id+"F0.wireOp",EDGE,"E56.1.13"),sQuery(id+"F0.wireOp",EDGE,"E56.1.14"),sQuery(id+"F0.wireOp",EDGE,"E56.1.15"),sQuery(id+"F0.wireOp",EDGE,"E56.1.16"),sQuery(id+"F0.wireOp",EDGE,"E56.1.17"),sQuery(id+"F0.wireOp",EDGE,"E56.1.18"),sQuery(id+"F0.wireOp",EDGE,"E56.1.19"),sQuery(id+"F0.wireOp",EDGE,"E56.1.20"),sQuery(id+"F0.wireOp",EDGE,"E56.1.21"),sQuery(id+"F0.wireOp",EDGE,"E56.1.22"),sQuery(id+"F0.wireOp",EDGE,"E56.1.23"),sQuery(id+"F0.wireOp",EDGE,"E56.1.24"),sQuery(id+"F0.wireOp",EDGE,"E56.1.25"),sQuery(id+"F0.wireOp",EDGE,"E56.1.26"),sQuery(id+"F0.wireOp",EDGE,"E56.1.27"),sQuery(id+"F0.wireOp",EDGE,"E56.1.28"),sQuery(id+"F0.wireOp",EDGE,"E56.1.29"),sQuery(id+"F0.wireOp",EDGE,"E56.1.30"),sQuery(id+"F0.wireOp",EDGE,"E56.1.31"),sQuery(id+"F0.wireOp",EDGE,"E56.1.32"),sQuery(id+"F0.wireOp",EDGE,"E56.1.33"),sQuery(id+"F0.wireOp",EDGE,"E56.1.34"),sQuery(id+"F0.wireOp",EDGE,"E56.1.35"),sQuery(id+"F0.wireOp",EDGE,"E56.1.36"),sQuery(id+"F0.wireOp",EDGE,"E56.1.37"),sQuery(id+"F0.wireOp",EDGE,"E56.1.38"),sQuery(id+"F0.wireOp",EDGE,"E56.1.47"),sQuery(id+"F0.wireOp",EDGE,"E56.1.48"),sQuery(id+"F0.wireOp",EDGE,"E56.1.49"),sQuery(id+"F0.wireOp",EDGE,"E56.1.50"),sQuery(id+"F0.wireOp",EDGE,"E56.1.51"),sQuery(id+"F0.wireOp",EDGE,"E56.1.52"),sQuery(id+"F0.wireOp",EDGE,"E56.2.0"),sQuery(id+"F0.wireOp",EDGE,"E56.2.1"),sQuery(id+"F0.wireOp",EDGE,"E56.2.2"),sQuery(id+"F0.wireOp",EDGE,"E56.2.3"),sQuery(id+"F0.wireOp",EDGE,"E56.2.4"),sQuery(id+"F0.wireOp",EDGE,"E56.2.5"),sQuery(id+"F0.wireOp",EDGE,"E56.2.6"),sQuery(id+"F0.wireOp",EDGE,"E56.2.7"),sQuery(id+"F0.wireOp",EDGE,"E56.2.8"),sQuery(id+"F0.wireOp",EDGE,"E56.2.9"),sQuery(id+"F0.wireOp",EDGE,"E56.2.10"),sQuery(id+"F0.wireOp",EDGE,"E56.2.11"),sQuery(id+"F0.wireOp",EDGE,"E56.2.12"),sQuery(id+"F0.wireOp",EDGE,"E56.2.13"),sQuery(id+"F0.wireOp",EDGE,"E56.2.14"),sQuery(id+"F0.wireOp",EDGE,"E56.2.15"),sQuery(id+"F0.wireOp",EDGE,"E56.2.16"),sQuery(id+"F0.wireOp",EDGE,"E56.2.17"),sQuery(id+"F0.wireOp",EDGE,"E56.2.18"),sQuery(id+"F0.wireOp",EDGE,"E56.2.19"),sQuery(id+"F0.wireOp",EDGE,"E56.2.20"),sQuery(id+"F0.wireOp",EDGE,"E56.2.21"),sQuery(id+"F0.wireOp",EDGE,"E56.2.22"),sQuery(id+"F0.wireOp",EDGE,"E56.2.23"),sQuery(id+"F0.wireOp",EDGE,"E56.2.24"),sQuery(id+"F0.wireOp",EDGE,"E56.2.25"),sQuery(id+"F0.wireOp",EDGE,"E56.2.26"),sQuery(id+"F0.wireOp",EDGE,"E56.2.27"),sQuery(id+"F0.wireOp",EDGE,"E56.2.28"),sQuery(id+"F0.wireOp",EDGE,"E56.2.29"),sQuery(id+"F0.wireOp",EDGE,"E56.2.30"),sQuery(id+"F0.wireOp",EDGE,"E56.2.31"),sQuery(id+"F0.wireOp",EDGE,"E56.2.32"),sQuery(id+"F0.wireOp",EDGE,"E56.2.33"),sQuery(id+"F0.wireOp",EDGE,"E56.2.34"),sQuery(id+"F0.wireOp",EDGE,"E56.2.35"),sQuery(id+"F0.wireOp",EDGE,"E56.2.36"),sQuery(id+"F0.wireOp",EDGE,"E56.2.37"),sQuery(id+"F0.wireOp",EDGE,"E56.2.38"),sQuery(id+"F0.wireOp",EDGE,"E56.2.47"),sQuery(id+"F0.wireOp",EDGE,"E56.2.48"),sQuery(id+"F0.wireOp",EDGE,"E56.2.49"),sQuery(id+"F0.wireOp",EDGE,"E56.2.50"),sQuery(id+"F0.wireOp",EDGE,"E56.2.51"),sQuery(id+"F0.wireOp",EDGE,"E56.2.52"),sQuery(id+"F0.wireOp",EDGE,"E56.3.0"),sQuery(id+"F0.wireOp",EDGE,"E56.3.1"),sQuery(id+"F0.wireOp",EDGE,"E56.3.2"),sQuery(id+"F0.wireOp",EDGE,"E56.3.3"),sQuery(id+"F0.wireOp",EDGE,"E56.3.4"),sQuery(id+"F0.wireOp",EDGE,"E56.3.5"),sQuery(id+"F0.wireOp",EDGE,"E56.3.6"),sQuery(id+"F0.wireOp",EDGE,"E56.3.7"),sQuery(id+"F0.wireOp",EDGE,"E56.3.8"),sQuery(id+"F0.wireOp",EDGE,"E56.3.9"),sQuery(id+"F0.wireOp",EDGE,"E56.3.10"),sQuery(id+"F0.wireOp",EDGE,"E56.3.11"),sQuery(id+"F0.wireOp",EDGE,"E56.3.12"),sQuery(id+"F0.wireOp",EDGE,"E56.3.13"),sQuery(id+"F0.wireOp",EDGE,"E56.3.14"),sQuery(id+"F0.wireOp",EDGE,"E56.3.15"),sQuery(id+"F0.wireOp",EDGE,"E56.3.16"),sQuery(id+"F0.wireOp",EDGE,"E56.3.17"),sQuery(id+"F0.wireOp",EDGE,"E56.3.18"),sQuery(id+"F0.wireOp",EDGE,"E56.3.19"),sQuery(id+"F0.wireOp",EDGE,"E56.3.20"),sQuery(id+"F0.wireOp",EDGE,"E56.3.21"),sQuery(id+"F0.wireOp",EDGE,"E56.3.22"),sQuery(id+"F0.wireOp",EDGE,"E56.3.23"),sQuery(id+"F0.wireOp",EDGE,"E56.3.24"),sQuery(id+"F0.wireOp",EDGE,"E56.3.25"),sQuery(id+"F0.wireOp",EDGE,"E56.3.26"),sQuery(id+"F0.wireOp",EDGE,"E56.3.27"),sQuery(id+"F0.wireOp",EDGE,"E56.3.28"),sQuery(id+"F0.wireOp",EDGE,"E56.3.29"),sQuery(id+"F0.wireOp",EDGE,"E56.3.30"),sQuery(id+"F0.wireOp",EDGE,"E56.3.31"),sQuery(id+"F0.wireOp",EDGE,"E56.3.32"),sQuery(id+"F0.wireOp",EDGE,"E56.3.33"),sQuery(id+"F0.wireOp",EDGE,"E56.3.34"),sQuery(id+"F0.wireOp",EDGE,"E56.3.35"),sQuery(id+"F0.wireOp",EDGE,"E56.3.36"),sQuery(id+"F0.wireOp",EDGE,"E56.3.37"),sQuery(id+"F0.wireOp",EDGE,"E56.3.38"),sQuery(id+"F0.wireOp",EDGE,"E56.3.47"),sQuery(id+"F0.wireOp",EDGE,"E56.3.48"),sQuery(id+"F0.wireOp",EDGE,"E56.3.49"),sQuery(id+"F0.wireOp",EDGE,"E56.3.50"),sQuery(id+"F0.wireOp",EDGE,"E56.3.51"),sQuery(id+"F0.wireOp",EDGE,"E56.3.52"),sQuery(id+"F0.wireOp",EDGE,"E56.4.0"),sQuery(id+"F0.wireOp",EDGE,"E56.4.1"),sQuery(id+"F0.wireOp",EDGE,"E56.4.2"),sQuery(id+"F0.wireOp",EDGE,"E56.4.3"),sQuery(id+"F0.wireOp",EDGE,"E56.4.4"),sQuery(id+"F0.wireOp",EDGE,"E56.4.5"),sQuery(id+"F0.wireOp",EDGE,"E56.4.6"),sQuery(id+"F0.wireOp",EDGE,"E56.4.7"),sQuery(id+"F0.wireOp",EDGE,"E56.4.8"),sQuery(id+"F0.wireOp",EDGE,"E56.4.9"),sQuery(id+"F0.wireOp",EDGE,"E56.4.10"),sQuery(id+"F0.wireOp",EDGE,"E56.4.11"),sQuery(id+"F0.wireOp",EDGE,"E56.4.12"),sQuery(id+"F0.wireOp",EDGE,"E56.4.13"),sQuery(id+"F0.wireOp",EDGE,"E56.4.14"),sQuery(id+"F0.wireOp",EDGE,"E56.4.15"),sQuery(id+"F0.wireOp",EDGE,"E56.4.16"),sQuery(id+"F0.wireOp",EDGE,"E56.4.17"),sQuery(id+"F0.wireOp",EDGE,"E56.4.18"),sQuery(id+"F0.wireOp",EDGE,"E56.4.19"),sQuery(id+"F0.wireOp",EDGE,"E56.4.20"),sQuery(id+"F0.wireOp",EDGE,"E56.4.21"),sQuery(id+"F0.wireOp",EDGE,"E56.4.22"),sQuery(id+"F0.wireOp",EDGE,"E56.4.23"),sQuery(id+"F0.wireOp",EDGE,"E56.4.24"),sQuery(id+"F0.wireOp",EDGE,"E56.4.25"),sQuery(id+"F0.wireOp",EDGE,"E56.4.26"),sQuery(id+"F0.wireOp",EDGE,"E56.4.27"),sQuery(id+"F0.wireOp",EDGE,"E56.4.28"),sQuery(id+"F0.wireOp",EDGE,"E56.4.29"),sQuery(id+"F0.wireOp",EDGE,"E56.4.30"),sQuery(id+"F0.wireOp",EDGE,"E56.4.31"),sQuery(id+"F0.wireOp",EDGE,"E56.4.32"),sQuery(id+"F0.wireOp",EDGE,"E56.4.33"),sQuery(id+"F0.wireOp",EDGE,"E56.4.34"),sQuery(id+"F0.wireOp",EDGE,"E56.4.35"),sQuery(id+"F0.wireOp",EDGE,"E56.4.36"),sQuery(id+"F0.wireOp",EDGE,"E56.4.37"),sQuery(id+"F0.wireOp",EDGE,"E56.4.38"),sQuery(id+"F0.wireOp",EDGE,"E56.4.47"),sQuery(id+"F0.wireOp",EDGE,"E56.4.48"),sQuery(id+"F0.wireOp",EDGE,"E56.4.49"),sQuery(id+"F0.wireOp",EDGE,"E56.4.50"),sQuery(id+"F0.wireOp",EDGE,"E56.4.51"),sQuery(id+"F0.wireOp",EDGE,"E56.4.52"),sQuery(id+"F0.wireOp",EDGE,"E56.5.0"),sQuery(id+"F0.wireOp",EDGE,"E56.5.1"),sQuery(id+"F0.wireOp",EDGE,"E56.5.2"),sQuery(id+"F0.wireOp",EDGE,"E56.5.3"),sQuery(id+"F0.wireOp",EDGE,"E56.5.4"),sQuery(id+"F0.wireOp",EDGE,"E56.5.5"),sQuery(id+"F0.wireOp",EDGE,"E56.5.6"),sQuery(id+"F0.wireOp",EDGE,"E56.5.7"),sQuery(id+"F0.wireOp",EDGE,"E56.5.8"),sQuery(id+"F0.wireOp",EDGE,"E56.5.9"),sQuery(id+"F0.wireOp",EDGE,"E56.5.10"),sQuery(id+"F0.wireOp",EDGE,"E56.5.11"),sQuery(id+"F0.wireOp",EDGE,"E56.5.12"),sQuery(id+"F0.wireOp",EDGE,"E56.5.13"),sQuery(id+"F0.wireOp",EDGE,"E56.5.14"),sQuery(id+"F0.wireOp",EDGE,"E56.5.15"),sQuery(id+"F0.wireOp",EDGE,"E56.5.16"),sQuery(id+"F0.wireOp",EDGE,"E56.5.17"),sQuery(id+"F0.wireOp",EDGE,"E56.5.18"),sQuery(id+"F0.wireOp",EDGE,"E56.5.19"),sQuery(id+"F0.wireOp",EDGE,"E56.5.20"),sQuery(id+"F0.wireOp",EDGE,"E56.5.21"),sQuery(id+"F0.wireOp",EDGE,"E56.5.22"),sQuery(id+"F0.wireOp",EDGE,"E56.5.23"),sQuery(id+"F0.wireOp",EDGE,"E56.5.24"),sQuery(id+"F0.wireOp",EDGE,"E56.5.25"),sQuery(id+"F0.wireOp",EDGE,"E56.5.26"),sQuery(id+"F0.wireOp",EDGE,"E56.5.27"),sQuery(id+"F0.wireOp",EDGE,"E56.5.28"),sQuery(id+"F0.wireOp",EDGE,"E56.5.29"),sQuery(id+"F0.wireOp",EDGE,"E56.5.30"),sQuery(id+"F0.wireOp",EDGE,"E56.5.31"),sQuery(id+"F0.wireOp",EDGE,"E56.5.32"),sQuery(id+"F0.wireOp",EDGE,"E56.5.33"),sQuery(id+"F0.wireOp",EDGE,"E56.5.34"),sQuery(id+"F0.wireOp",EDGE,"E56.5.35"),sQuery(id+"F0.wireOp",EDGE,"E56.5.36"),sQuery(id+"F0.wireOp",EDGE,"E56.5.37"),sQuery(id+"F0.wireOp",EDGE,"E56.5.38"),sQuery(id+"F0.wireOp",EDGE,"E56.5.47"),sQuery(id+"F0.wireOp",EDGE,"E56.5.48"),sQuery(id+"F0.wireOp",EDGE,"E56.5.49"),sQuery(id+"F0.wireOp",EDGE,"E56.5.50"),sQuery(id+"F0.wireOp",EDGE,"E56.5.51"),sQuery(id+"F0.wireOp",EDGE,"E56.5.52")])]});
            var Q1;
            Q1=qCreatedBy(makeId("Origin.pointOp"),VERTEX);
            transform(context, id + "F2", {"entities" : qUnion([Q0]), "transformType" : TransformType.SCALE_UNIFORMLY, "scale" : 2, "scalePoint" : qUnion([Q1]), "makeCopy" : false});
        }
    });
